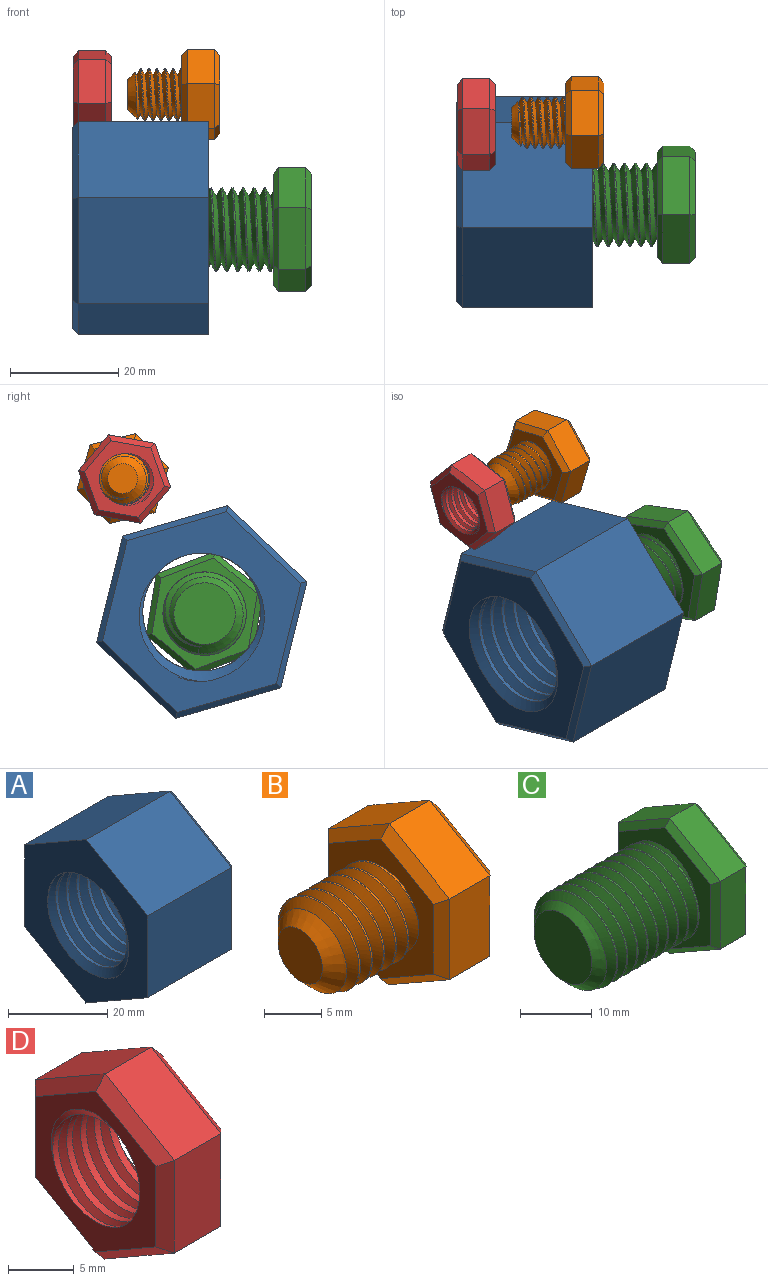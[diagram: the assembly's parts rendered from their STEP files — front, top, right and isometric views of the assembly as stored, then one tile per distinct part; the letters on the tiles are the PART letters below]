
ASSEMBLY  parts=4 mates=2
PART A: 17 faces, bbox 29x36.3x41.6 mm
  f0: cylinder r=10.88mm len=25mm, axis (1,0,0), area 496.3mm2, adj f7,f8,f15,f16
  f1: plane 24x17.48mm, normal (0,-0.5,0.87), area 485mm2, adj f2,f6,f7,f12
  f2: plane 24x20.21mm, normal (0,-1,0), area 485mm2, adj f1,f3,f7,f10
  f3: plane 24x17.52mm, normal (0,-0.5,-0.87), area 485mm2, adj f2,f4,f7,f9
  f4: plane 24x17.48mm, normal (0,0.5,-0.87), area 485mm2, adj f3,f5,f7,f11
  f5: plane 24x20.21mm, normal (0,1,0), area 485mm2, adj f4,f6,f7,f13
  f6: plane 24x17.52mm, normal (0,0.5,0.87), area 485mm2, adj f1,f5,f7,f14
  f7: plane 41.63x36.25mm, normal (-1,0,0), area 636.2mm2, adj f0,f1,f2,f3,f4,f5,f6,f15
  f8: plane 39.32x34.25mm, normal (1,0,0), area 518.5mm2, adj f0,f9,f10,f11,f12,f13,f14,f15
  f9: plane 17.52x10.65mm, normal (0.71,-0.35,-0.61), area 27.8mm2, adj f3,f8,f10,f11
  f10: plane 20.21x1.04mm, normal (0.71,-0.71,0), area 27.8mm2, adj f2,f8,f9,f12
  f11: plane 17.48x10.71mm, normal (0.71,0.35,-0.61), area 27.8mm2, adj f4,f8,f9,f13
  f12: plane 17.48x10.71mm, normal (0.71,-0.35,0.61), area 27.8mm2, adj f1,f8,f10,f14
  f13: plane 20.21x1.04mm, normal (0.71,0.71,0), area 27.8mm2, adj f5,f8,f11,f14
  f14: plane 17.52x10.65mm, normal (0.71,0.35,0.61), area 27.8mm2, adj f6,f8,f12,f13
  f15: bspline ~29.62x27.63mm, area 1396.8mm2, adj f0,f7,f8,f16
  f16: bspline ~29.62x27.63mm, area 1398.5mm2, adj f0,f7,f8,f15
PART B: 25 faces, bbox 17.8x15.9x18.1 mm
  f0: cylinder r=4.75mm len=9.5mm, axis (1,0,0), area 28.1mm2, adj f1,f2,f4,f12
  f1: bspline ~10.97x9.91mm, area 196.7mm2, adj f0,f2,f4,f12
  f2: bspline ~10.97x10.66mm, area 196.6mm2, adj f0,f1,f4,f12
  f3: plane 5.5x5.5mm, normal (-1,0,0), area 23.8mm2, adj f4
  f4: cone r=4.75mm half-angle=45deg, axis (1,0,0), area 47.4mm2, adj f0,f1,f2,f3
  f5: plane 7.48x5mm, normal (0,-0.5,0.86), area 43.3mm2, adj f6,f10,f18,f22
  f6: plane 8.66x5mm, normal (0,-1,0), area 43.3mm2, adj f5,f7,f16,f20
  f7: plane 7.52x5mm, normal (0,-0.5,-0.87), area 43.3mm2, adj f6,f8,f14,f19
  f8: plane 7.48x5mm, normal (0,0.5,-0.86), area 43.3mm2, adj f7,f9,f13,f21
  f9: plane 8.66x5mm, normal (0,1,0), area 43.3mm2, adj f8,f10,f15,f23
  f10: plane 7.52x5mm, normal (0,0.5,0.87), area 43.3mm2, adj f5,f9,f17,f24
  f11: plane 15.01x13.03mm, normal (1,0,0), area 146.4mm2, adj f13,f14,f15,f16,f17,f18
  f12: plane 15.83x13.85mm, normal (-1,0,0), area 89.2mm2, adj f0,f1,f2,f19,f20,f21,f22,f23
  f13: plane 7.49x4.93mm, normal (0.71,0.36,-0.61), area 11.4mm2, adj f8,f11,f14,f15
  f14: plane 7.52x4.88mm, normal (0.71,-0.35,-0.61), area 11.4mm2, adj f7,f11,f13,f16
  f15: plane 8.66x1.03mm, normal (0.71,0.71,0), area 11.4mm2, adj f9,f11,f13,f17
  f16: plane 8.66x1.03mm, normal (0.71,-0.71,0), area 11.4mm2, adj f6,f11,f14,f18
  f17: plane 7.52x4.88mm, normal (0.71,0.35,0.61), area 11.4mm2, adj f10,f11,f15,f18
  f18: plane 7.49x4.93mm, normal (0.71,-0.36,0.61), area 11.4mm2, adj f5,f11,f16,f17
  f19: plane 7.52x4.88mm, normal (-0.71,-0.35,-0.61), area 11.4mm2, adj f7,f12,f20,f21
  f20: plane 8.66x1.03mm, normal (-0.71,-0.71,0), area 11.4mm2, adj f6,f12,f19,f22
  f21: plane 7.49x4.93mm, normal (-0.71,0.36,-0.61), area 11.4mm2, adj f8,f12,f19,f23
  f22: plane 7.49x4.93mm, normal (-0.71,-0.36,0.61), area 11.4mm2, adj f5,f12,f20,f24
  f23: plane 8.66x1.03mm, normal (-0.71,0.71,0), area 11.4mm2, adj f9,f12,f21,f24
  f24: plane 7.52x4.88mm, normal (-0.71,0.35,0.61), area 11.4mm2, adj f10,f12,f22,f23
PART C: 26 faces, bbox 27.7x20x23.1 mm
  f0: cylinder r=7.68mm len=18mm, axis (1,0,0), area 139.1mm2, adj f1,f2,f5,f13
  f1: bspline ~20.88x17.74mm, area 713.8mm2, adj f0,f2,f4,f5,f13
  f2: bspline ~21.88x17.74mm, area 715.1mm2, adj f0,f1,f4,f5,f13
  f3: plane 11.36x11.36mm, normal (-1,0,0), area 101.4mm2, adj f4
  f4: cone r=7.68mm half-angle=45deg, axis (1,0,0), area 63.2mm2, adj f1,f2,f3,f5
  f5: cone r=7.68mm half-angle=45deg, axis (1,0,0), area 13.2mm2, adj f0,f1,f2,f4
  f6: plane 9.98x5.81mm, normal (0,-0.5,0.86), area 57.7mm2, adj f7,f11,f19,f23
  f7: plane 11.55x5mm, normal (0,-1,0), area 57.7mm2, adj f6,f8,f17,f21
  f8: plane 10.02x5.74mm, normal (0,-0.5,-0.87), area 57.7mm2, adj f7,f9,f15,f20
  f9: plane 9.98x5.81mm, normal (0,0.5,-0.86), area 57.7mm2, adj f8,f10,f14,f22
  f10: plane 11.55x5mm, normal (0,1,0), area 57.7mm2, adj f9,f11,f16,f24
  f11: plane 10.02x5.74mm, normal (0,0.5,0.87), area 57.7mm2, adj f6,f10,f18,f25
  f12: plane 20.78x18.04mm, normal (1,0,0), area 280.6mm2, adj f14,f15,f16,f17,f18,f19
  f13: plane 20.78x18.04mm, normal (-1,0,0), area 125.2mm2, adj f0,f1,f2,f20,f21,f22,f23,f24
  f14: plane 9.98x6.38mm, normal (0.71,0.36,-0.61), area 15.5mm2, adj f9,f12,f15,f16
  f15: plane 10.02x6.32mm, normal (0.71,-0.35,-0.61), area 15.5mm2, adj f8,f12,f14,f17
  f16: plane 11.55x1.04mm, normal (0.71,0.71,0), area 15.5mm2, adj f10,f12,f14,f18
  f17: plane 11.55x1.04mm, normal (0.71,-0.71,0), area 15.5mm2, adj f7,f12,f15,f19
  f18: plane 10.02x6.32mm, normal (0.71,0.35,0.61), area 15.5mm2, adj f11,f12,f16,f19
  f19: plane 9.98x6.38mm, normal (0.71,-0.36,0.61), area 15.5mm2, adj f6,f12,f17,f18
  f20: plane 10.02x6.32mm, normal (-0.71,-0.35,-0.61), area 15.5mm2, adj f8,f13,f21,f22
  f21: plane 11.55x1.04mm, normal (-0.71,-0.71,0), area 15.5mm2, adj f7,f13,f20,f23
  f22: plane 9.98x6.38mm, normal (-0.71,0.36,-0.61), area 15.5mm2, adj f9,f13,f20,f24
  f23: plane 9.98x6.38mm, normal (-0.71,-0.36,0.61), area 15.5mm2, adj f6,f13,f21,f25
  f24: plane 11.55x1.04mm, normal (-0.71,0.71,0), area 15.5mm2, adj f10,f13,f22,f25
  f25: plane 10.02x6.32mm, normal (-0.71,0.35,0.61), area 15.5mm2, adj f11,f13,f23,f24
PART D: 23 faces, bbox 9.1x15.4x17.7 mm
  f0: plane 7.49x5mm, normal (0,-0.5,0.86), area 43.3mm2, adj f1,f5,f13,f17
  f1: plane 8.66x5mm, normal (0,-1,0), area 43.3mm2, adj f0,f2,f11,f15
  f2: plane 7.51x5mm, normal (0,-0.5,-0.87), area 43.3mm2, adj f1,f3,f9,f14
  f3: plane 7.49x5mm, normal (0,0.5,-0.86), area 43.3mm2, adj f2,f4,f8,f16
  f4: plane 8.66x5mm, normal (0,1,0), area 43.3mm2, adj f3,f5,f10,f18
  f5: plane 7.51x5mm, normal (0,0.5,0.87), area 43.3mm2, adj f0,f4,f12,f19
  f6: plane 15.37x13.38mm, normal (-1,0,0), area 71.4mm2, adj f8,f9,f10,f11,f12,f13,f20,f21
  f7: plane 15.37x13.38mm, normal (1,0,0), area 71.4mm2, adj f14,f15,f16,f17,f18,f19,f20,f21
  f8: plane 7.49x4.93mm, normal (-0.71,0.36,-0.61), area 11.4mm2, adj f3,f6,f9,f10
  f9: plane 7.51x4.89mm, normal (-0.71,-0.35,-0.61), area 11.4mm2, adj f2,f6,f8,f11
  f10: plane 8.66x1.02mm, normal (-0.71,0.71,0), area 11.4mm2, adj f4,f6,f8,f12
  f11: plane 8.66x1.02mm, normal (-0.71,-0.71,0), area 11.4mm2, adj f1,f6,f9,f13
  f12: plane 7.51x4.89mm, normal (-0.71,0.35,0.61), area 11.4mm2, adj f5,f6,f10,f13
  f13: plane 7.49x4.93mm, normal (-0.71,-0.36,0.61), area 11.4mm2, adj f0,f6,f11,f12
  f14: plane 7.51x4.89mm, normal (0.71,-0.35,-0.61), area 11.4mm2, adj f2,f7,f15,f16
  f15: plane 8.66x1.02mm, normal (0.71,-0.71,0), area 11.4mm2, adj f1,f7,f14,f17
  f16: plane 7.49x4.93mm, normal (0.71,0.36,-0.61), area 11.4mm2, adj f3,f7,f14,f18
  f17: plane 7.49x4.93mm, normal (0.71,-0.36,0.61), area 11.4mm2, adj f0,f7,f15,f19
  f18: plane 8.66x1.02mm, normal (0.71,0.71,0), area 11.4mm2, adj f4,f7,f16,f19
  f19: plane 7.51x4.89mm, normal (0.71,0.35,0.61), area 11.4mm2, adj f5,f7,f17,f18
  f20: cylinder r=4.66mm len=9.32mm, axis (1,0,0), area 85.4mm2, adj f6,f7,f21,f22
  f21: bspline ~12.5x10.82mm, area 128.4mm2, adj f6,f7,f20,f22
  f22: bspline ~12.5x10.82mm, area 128.5mm2, adj f6,f7,f20,f21
PLACE A rot(axis=(0,0.6,-0.8),180deg) t=(-55.27,-6.86,23.48)mm fixed
PLACE B rot(axis=(-1,0,0),43.8deg) t=(-31.66,7.73,48.08)mm
PLACE C rot(axis=(1,0,0),9.1deg) t=(-14.77,-7.39,23.19)mm
PLACE D rot(axis=(1,0,0),100.2deg) t=(-48.16,7.38,48.02)mm fixed
MATE cylindrical C.f0 <-> A.f7  axis (-1,0,0) through (-38.27,-7.39,23.19)mm
MATE cylindrical B.f0 <-> D.f6  axis (-1,0,0) through (-45.16,7.73,48.08)mm
